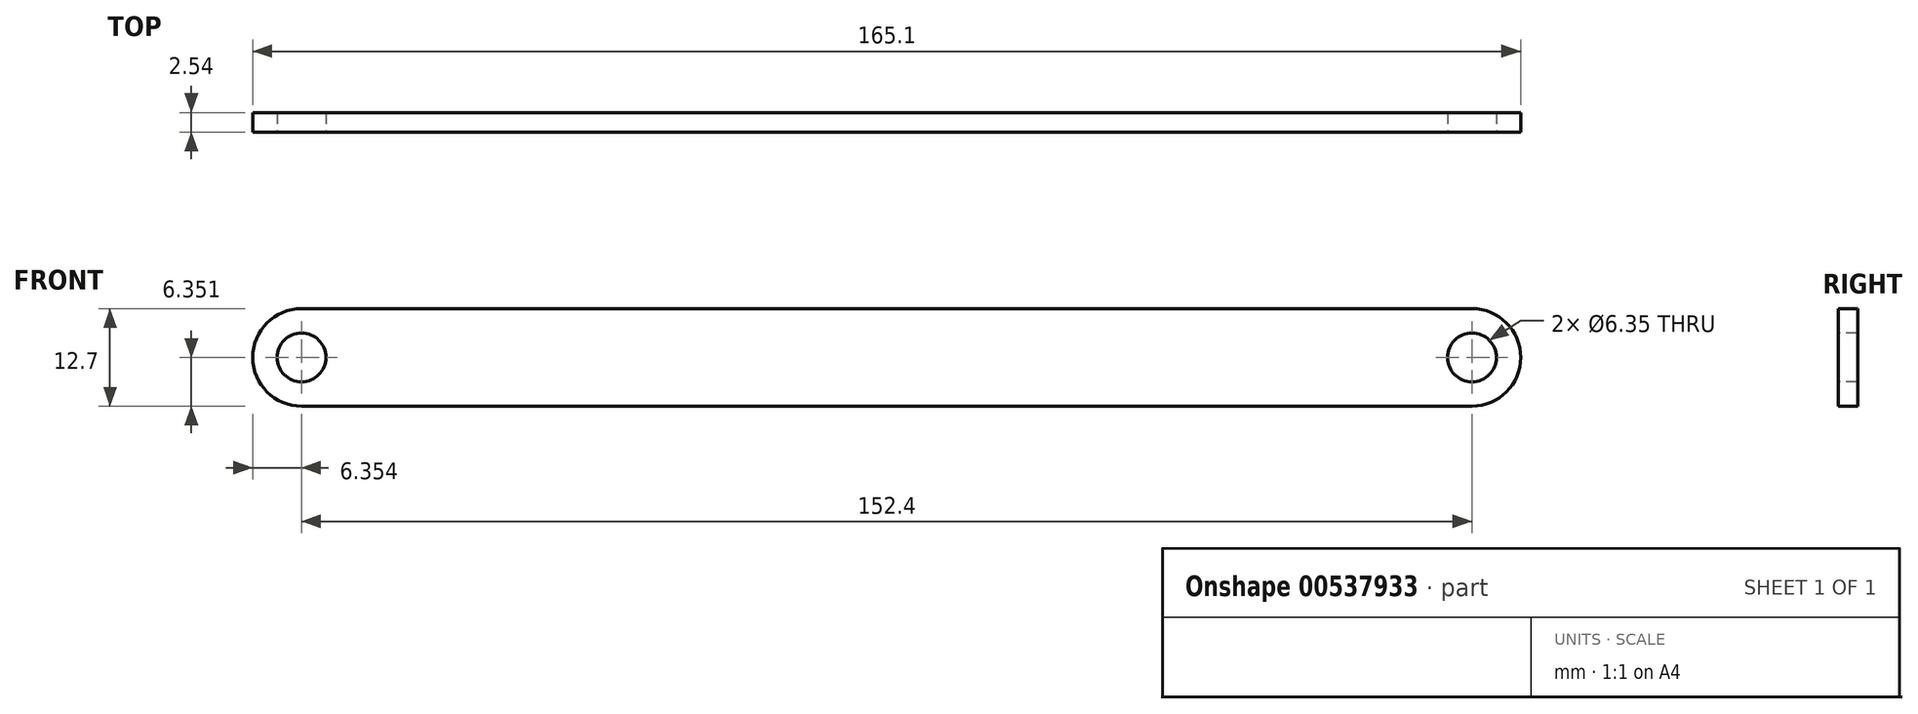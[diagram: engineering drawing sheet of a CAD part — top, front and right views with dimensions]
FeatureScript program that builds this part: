
annotation { "Feature Type Name" : "Feature", "Feature Type Description" : "" }
export const myFeature = defineFeature(function(context is Context, id is Id, definition is map)
    precondition{}
    {
        {
            var Q0;
            Q0=qCreatedBy(makeId("Front.planeOp"),FACE);
            var sketch = newSketch(context, id + "F0", { "sketchPlane" : qUnion([Q0])});
            skLineSegment(sketch, "E0", {"start": v(-95.14, -5.09) * mm, "end": v(57.26, -5.09) * mm});
            skLineSegment(sketch, "E1", {"start": v(63.61, 1.26) * mm, "end": v(63.61, 1.26) * mm});
            skLineSegment(sketch, "E2", {"start": v(57.26, 7.61) * mm, "end": v(-95.14, 7.61) * mm});
            skLineSegment(sketch, "E3", {"start": v(-101.49, 1.26) * mm, "end": v(-101.49, 1.26) * mm});
            skPoint(sketch, "E4.centerSnap0", {"position": v(-101.49, 1.26) * mm});
            skPoint(sketch, "E5.centerSnap0", {"position": v(63.61, 1.26) * mm});
            skPoint(sketch, "E6.visualSharp", {"position": v(-101.49, 7.61) * mm});
            skArc(sketch, "E6.filletArc", {"start": v(-95.14, 7.61) * mm, "mid": v(-99.63, 5.75) * mm, "end": v(-101.49, 1.26) * mm});
            skPoint(sketch, "E7.visualSharp", {"position": v(-101.49, -5.09) * mm});
            skArc(sketch, "E7.filletArc", {"start": v(-101.49, 1.26) * mm, "mid": v(-99.63, -3.23) * mm, "end": v(-95.14, -5.09) * mm});
            skPoint(sketch, "E8.visualSharp", {"position": v(63.61, 7.61) * mm});
            skArc(sketch, "E8.filletArc", {"start": v(63.61, 1.26) * mm, "mid": v(61.75, 5.75) * mm, "end": v(57.26, 7.61) * mm});
            skPoint(sketch, "E9.visualSharp", {"position": v(63.61, -5.09) * mm});
            skArc(sketch, "E9.filletArc", {"start": v(57.26, -5.09) * mm, "mid": v(61.75, -3.23) * mm, "end": v(63.61, 1.26) * mm});
            skSolve(sketch);
        }
        {
            var Q0;
            Q0 = qSketchRegion(id + "F0", true);
            extrude(context, id + "F1", {"entities" : qUnion([Q0]), "depth" : 2.54 * mm, "offsetDistance" : 25.4 * mm});
        }
        {
            var Q0;
            Q0=makeQuery(id+"F1.opExtrude","CAP_FACE",FACE,{"disambiguationData":[OSD([sQuery(id+"F0.wireOp",EDGE,"E0"),sQuery(id+"F0.wireOp",EDGE,"E2"),sQuery(id+"F0.wireOp",EDGE,"E6.filletArc"),sQuery(id+"F0.wireOp",EDGE,"E7.filletArc"),sQuery(id+"F0.wireOp",EDGE,"E8.filletArc"),sQuery(id+"F0.wireOp",EDGE,"E9.filletArc")])],"isStart":false});
            var sketch = newSketch(context, id + "F2", { "sketchPlane" : qUnion([Q0])});
            skCircle(sketch, "E10", {"center": v(-95.14, 1.26) * mm, "radius": 3.18 * mm});
            skCircle(sketch, "E11", {"center": v(57.26, 1.26) * mm, "radius": 3.18 * mm});
            skSolve(sketch);
        }
        {
            var Q0;
            Q0 = qSketchRegion(id + "F2", true);
            extrude(context, id + "F3", {"entities" : qUnion([Q0]), "operationType" : NewBodyOperationType.REMOVE, "endBound" : BoundingType.THROUGH_ALL, "oppositeDirection" : true, "depth" : 25.4 * mm, "offsetDistance" : 25.4 * mm});
        }
    });
